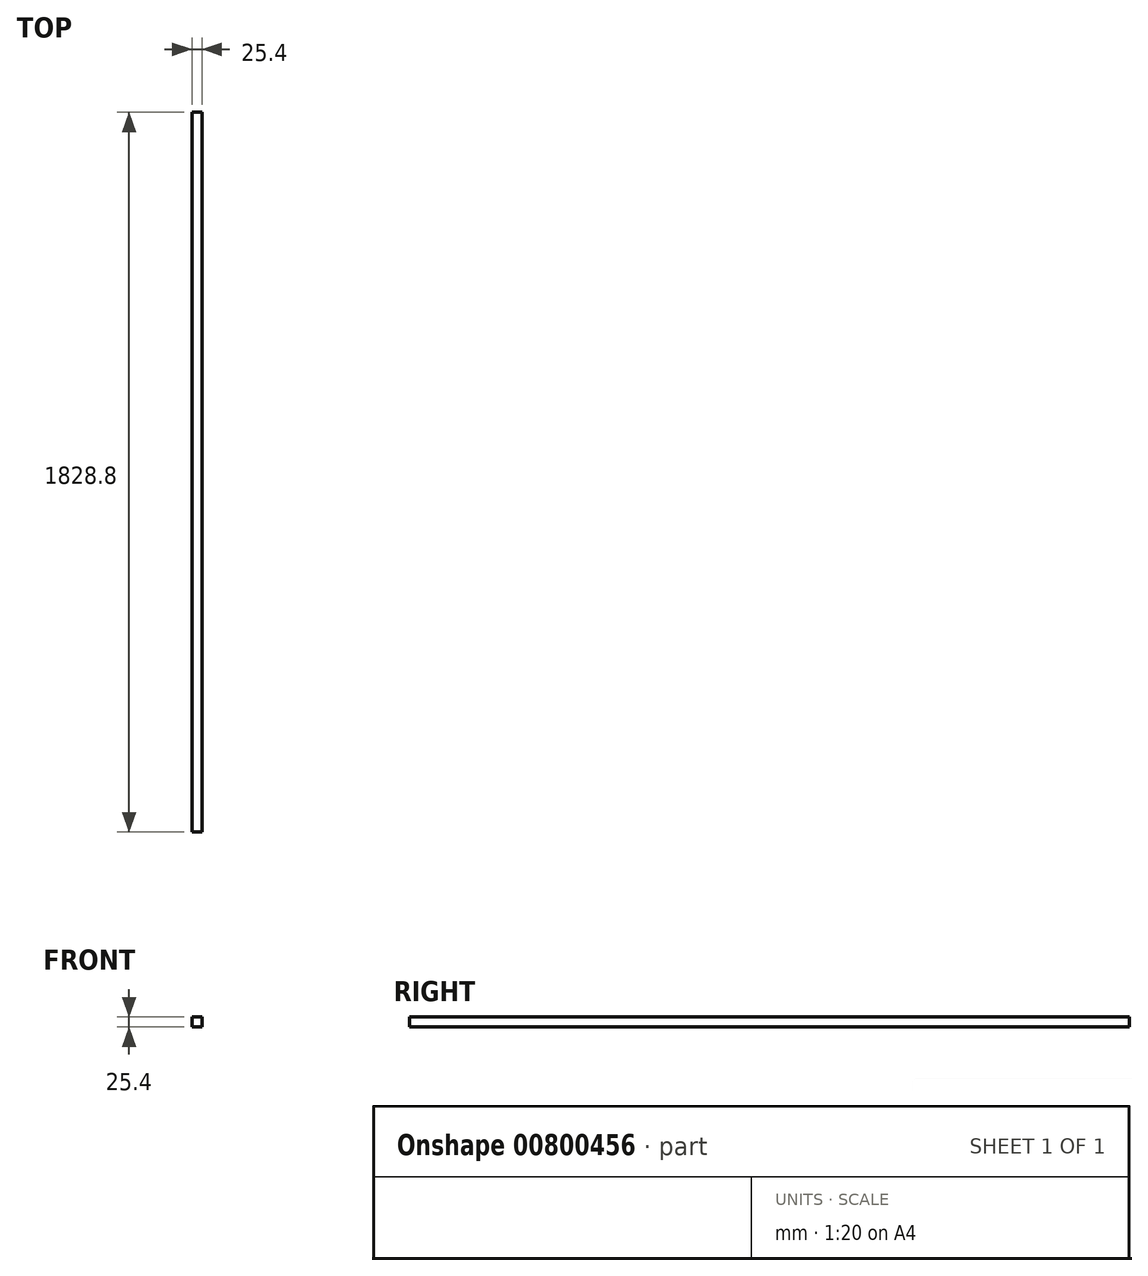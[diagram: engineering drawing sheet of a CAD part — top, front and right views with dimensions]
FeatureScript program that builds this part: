
annotation { "Feature Type Name" : "Feature", "Feature Type Description" : "" }
export const myFeature = defineFeature(function(context is Context, id is Id, definition is map)
    precondition{}
    {
        {
            var Q0;
            Q0=qCreatedBy(makeId("Front.planeOp"),FACE);
            var sketch = newSketch(context, id + "F0", { "sketchPlane" : qUnion([Q0])});
            skLineSegment(sketch, "E0.bottom", {"start": v(-79.46, 49.35) * mm, "end": v(-54.06, 49.35) * mm});
            skLineSegment(sketch, "E0.top", {"start": v(-79.46, 23.95) * mm, "end": v(-54.06, 23.95) * mm});
            skLineSegment(sketch, "E0.left", {"start": v(-79.46, 49.35) * mm, "end": v(-79.46, 23.95) * mm});
            skLineSegment(sketch, "E0.right", {"start": v(-54.06, 49.35) * mm, "end": v(-54.06, 23.95) * mm});
            skSolve(sketch);
        }
        {
            var Q0;
            Q0 = qSketchRegion(id + "F0", true);
            extrude(context, id + "F1", {"entities" : qUnion([Q0]), "depth" : 1828.8 * mm, "offsetDistance" : 25.4 * mm});
        }
    });
